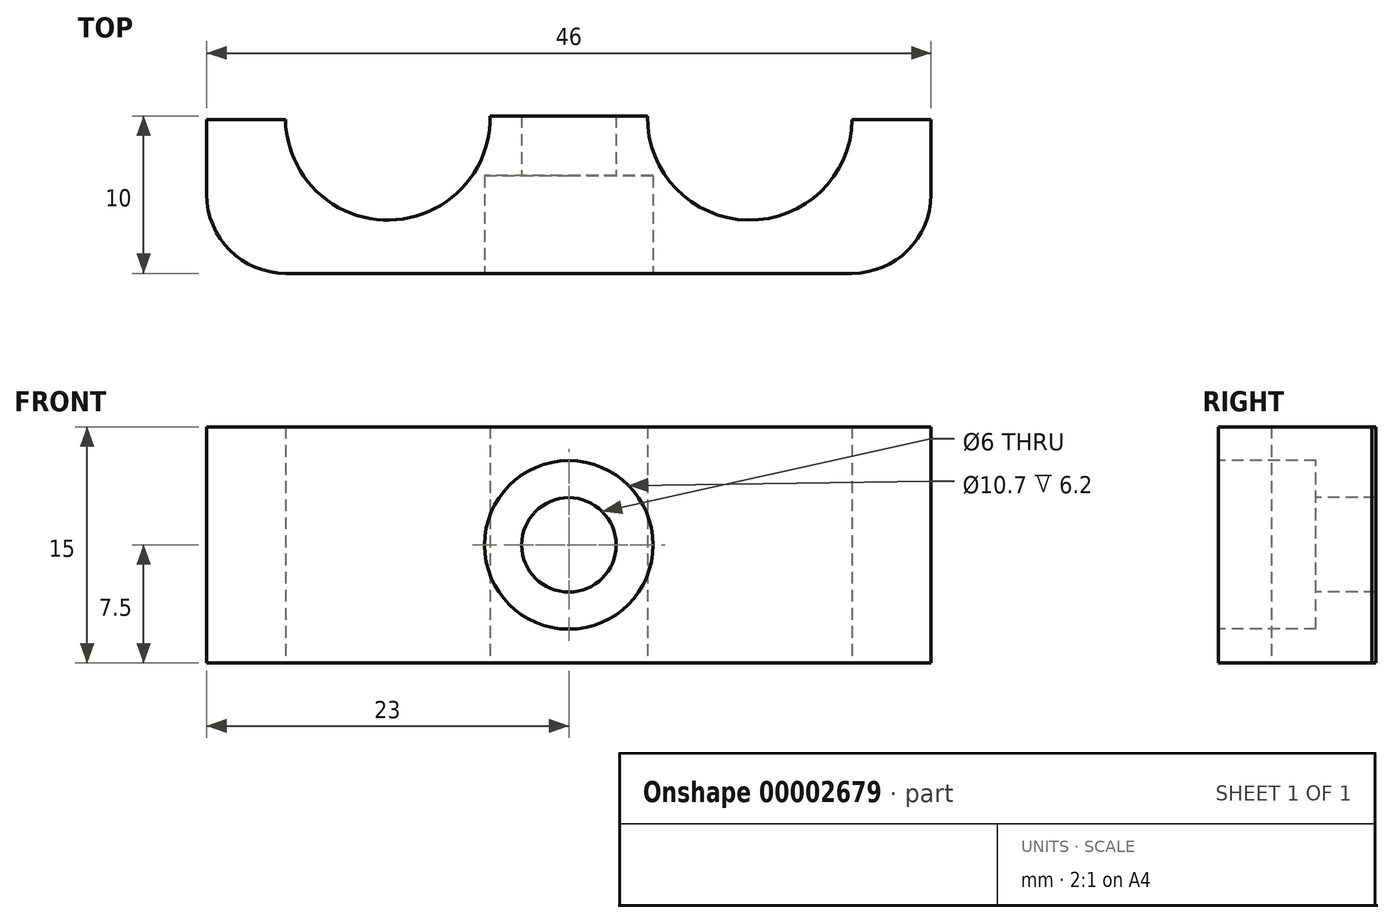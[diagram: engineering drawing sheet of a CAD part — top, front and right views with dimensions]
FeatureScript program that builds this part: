
annotation { "Feature Type Name" : "Feature", "Feature Type Description" : "" }
export const myFeature = defineFeature(function(context is Context, id is Id, definition is map)
    precondition{}
    {
        {
            var Q0;
            Q0=qCreatedBy(makeId("Top.planeOp"),FACE);
            var sketch = newSketch(context, id + "F0", { "sketchPlane" : qUnion([Q0])});
            skArc(sketch, "E0", {"start": v(-18.45, 22.31) * mm, "mid": v(-12.07, 15.7) * mm, "end": v(-5.45, 22.07) * mm});
            skLineSegment(sketch, "E1", {"start": v(-18.45, 22.31) * mm, "end": v(-23.45, 22.31) * mm});
            skLineSegment(sketch, "E2", {"start": v(-23.45, 12.31) * mm, "end": v(-5.45, 12.31) * mm});
            skLineSegment(sketch, "E3", {"start": v(-0.45, 17.31) * mm, "end": v(-0.45, 22.07) * mm});
            skPoint(sketch, "E4.visualSharp", {"position": v(-0.45, 12.31) * mm});
            skArc(sketch, "E4.filletArc", {"start": v(-5.45, 12.31) * mm, "mid": v(-1.92, 13.78) * mm, "end": v(-0.45, 17.31) * mm});
            skLineSegment(sketch, "E5", {"start": v(-5.45, 22.07) * mm, "end": v(-0.45, 22.07) * mm});
            skArc(sketch, "E6.MirrorCS", {"start": v(-28.45, 22.31) * mm, "mid": v(-34.83, 15.7) * mm, "end": v(-41.45, 22.07) * mm});
            skLineSegment(sketch, "E7.MirrorCS", {"start": v(-28.45, 22.31) * mm, "end": v(-23.45, 22.31) * mm});
            skLineSegment(sketch, "E8.MirrorCS", {"start": v(-23.45, 12.31) * mm, "end": v(-41.45, 12.31) * mm});
            skArc(sketch, "E9.MirrorCS", {"start": v(-41.45, 12.31) * mm, "mid": v(-44.98, 13.78) * mm, "end": v(-46.45, 17.31) * mm});
            skLineSegment(sketch, "E10.MirrorCS", {"start": v(-46.45, 17.31) * mm, "end": v(-46.45, 22.07) * mm});
            skLineSegment(sketch, "E11.MirrorCS", {"start": v(-41.45, 22.07) * mm, "end": v(-46.45, 22.07) * mm});
            skSolve(sketch);
        }
        {
            var Q0;
            Q0=makeQuery(id+"F0.imprint","IMPRINT",FACE,{"disambiguationData":[TD([[makeQuery(id+"F0.imprint","IMPRINT",EDGE,{"derivedFrom":sQuery(id+"F0.wireOp",EDGE,"E0")}),-1.0]])]});
            extrude(context, id + "F1", {"entities" : qUnion([Q0]), "depth" : 15 * mm});
        }
        {
            var Q0;
            Q0=makeQuery(id+"F1.opExtrude","SWEPT_FACE",FACE,{"disambiguationData":[OSD([sQuery(id+"F0.wireOp",EDGE,"E2"),sQuery(id+"F0.wireOp",EDGE,"E8.MirrorCS")])]});
            var sketch = newSketch(context, id + "F2", { "sketchPlane" : qUnion([Q0])});
            skLineSegment(sketch, "E12", {"start": v(-23.45, 15) * mm, "end": v(-23.45, 0) * mm});
            skPoint(sketch, "E13.0.midPoint", {"position": v(-23.45, 12.5) * mm});
            skCircle(sketch, "E14", {"center": v(-23.45, 7.5) * mm, "radius": 3 * mm});
            skCircle(sketch, "E15", {"center": v(-23.45, 7.5) * mm, "radius": 5.35 * mm});
            skPoint(sketch, "E16.orphan", {"position": v(-20.56, 2.5) * mm});
            skPoint(sketch, "E17.orphan", {"position": v(-20.56, 12.5) * mm});
            skPoint(sketch, "E18.trimOffspring.end.orphan", {"position": v(-26.34, 12.5) * mm});
            skSolve(sketch);
        }
        {
            var Q0;
            {var subQ0=sQuery(id+"F2.wireOp",EDGE,"E14");var subQ1=sQuery(id+"F2.wireOp",EDGE,"E12");var subQ2=makeQuery(id+"F2.imprint","INTERSECT",VERTEX,{"disambiguationData":[OD(0.0)],"derivedFrom":[subQ1,subQ0]});Q0=makeQuery(id+"F2.imprint","IMPRINT",FACE,{"disambiguationData":[TD([[makeQuery(id+"F2.imprint","IMPRINT",EDGE,{"disambiguationData":[TD([[subQ2,-1.0]])],"derivedFrom":subQ1}),1.0]])]});}
            var Q1;
            {var subQ0=sQuery(id+"F2.wireOp",EDGE,"E14");var subQ1=sQuery(id+"F2.wireOp",EDGE,"E12");var subQ2=makeQuery(id+"F2.imprint","INTERSECT",VERTEX,{"disambiguationData":[OD(0.0)],"derivedFrom":[subQ1,subQ0]});Q1=makeQuery(id+"F2.imprint","IMPRINT",FACE,{"disambiguationData":[TD([[makeQuery(id+"F2.imprint","IMPRINT",EDGE,{"disambiguationData":[TD([[subQ2,-1.0]])],"derivedFrom":subQ1}),-1.0]])]});}
            extrude(context, id + "F3", {"entities" : qUnion([Q0, Q1]), "operationType" : NewBodyOperationType.REMOVE, "oppositeDirection" : true, "depth" : 25 * mm});
        }
        {
            var Q0;
            Q0 = qSketchRegion(id + "F2", true);
            extrude(context, id + "F4", {"entities" : qUnion([Q0]), "operationType" : NewBodyOperationType.REMOVE, "oppositeDirection" : true, "depth" : 6.2 * mm});
        }
    });
